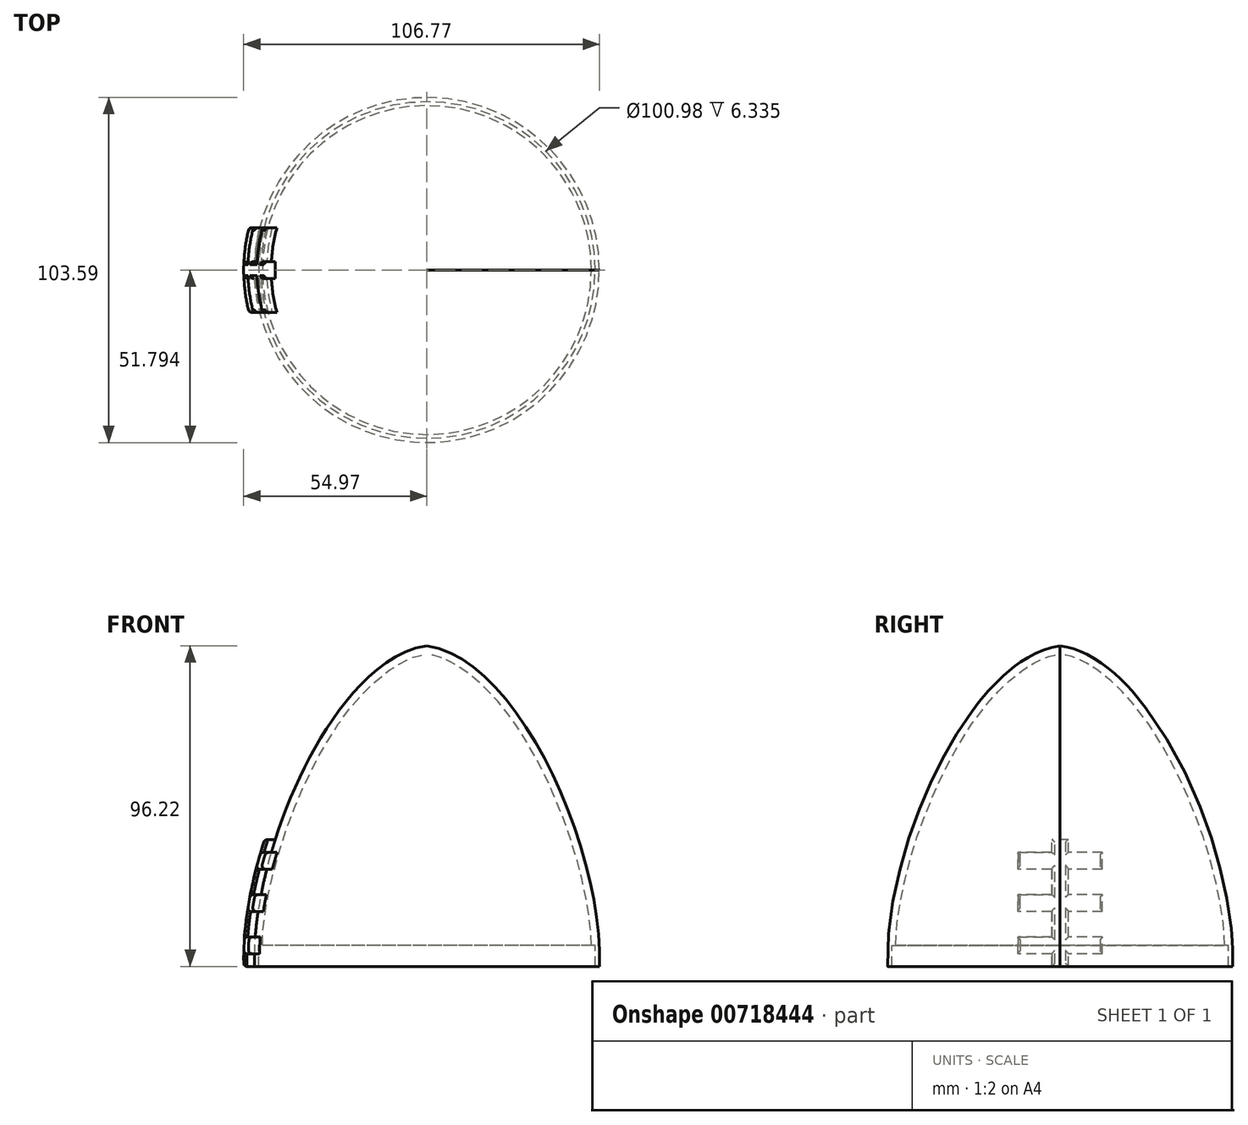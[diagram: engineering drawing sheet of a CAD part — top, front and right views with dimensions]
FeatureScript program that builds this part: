
annotation { "Feature Type Name" : "Feature", "Feature Type Description" : "" }
export const myFeature = defineFeature(function(context is Context, id is Id, definition is map)
    precondition{}
    {
        {
            var Q0;
            Q0=qCreatedBy(makeId("Front.planeOp"),FACE);
            var sketch = newSketch(context, id + "F0", { "sketchPlane" : qUnion([Q0])});
            skFitSpline(sketch, "E0", {"points": [v(40.85, 0) * mm, v(0, 75.94) * mm], "startDerivative": vector(2.97, 83.82) * mm, "endDerivative": vector(-64.34, 8.5) * mm});
            skFitSpline(sketch, "E1.0", {"points": [v(38.85, 0.07) * mm, v(38.97, 3.43) * mm, v(38.56, 10.75) * mm, v(36.21, 22.71) * mm, v(32.35, 34.94) * mm, v(27.22, 46.68) * mm, v(21.08, 57.23) * mm, v(15.35, 64.42) * mm, v(10.56, 68.85) * mm, v(6.92, 71.43) * mm, v(3.3, 73.2) * mm, v(0.92, 73.8) * mm, v(-0.26, 73.96) * mm]});
            skLineSegment(sketch, "E2", {"start": v(0, 75.94) * mm, "end": v(0, 73.92) * mm});
            skLineSegment(sketch, "E3", {"start": v(40.85, 0) * mm, "end": v(38.85, 0) * mm});
            skLineSegment(sketch, "E4", {"start": v(38.85, 0.07) * mm, "end": v(38.85, 0) * mm});
            skLineSegment(sketch, "E5", {"start": v(0, 73.92) * mm, "end": v(0, 73.92) * mm});
            skLineSegment(sketch, "E6", {"start": v(0, 77.78) * mm, "end": v(0, 26.3) * mm, "construction": true});
            skPoint(sketch, "E6.endSnap0", {"position": v(0, 74.93) * mm});
            skLineSegment(sketch, "E7", {"start": v(39.85, 0) * mm, "end": v(39.85, 5) * mm});
            skLineSegment(sketch, "E8", {"start": v(39.85, 5) * mm, "end": v(38.77, 5) * mm});
            skSolve(sketch);
        }
        {
            var Q0;
            Q0=makeQuery(id+"F0.imprint","IMPRINT",FACE,{"disambiguationData":[TD([[makeQuery(id+"F0.imprint","IMPRINT",EDGE,{"derivedFrom":sQuery(id+"F0.wireOp",EDGE,"E0")}),1.0]])]});
            var Q1;
            Q1=sQuery(id+"F0.wireOp",EDGE,"E6");
            revolve(context, id + "F1", {"surfaceOperationType" : NewSurfaceOperationType.NEW, "entities" : qUnion([Q0]), "axis" : qUnion([Q1]), "revolveType" : RevolveType.FULL});
        }
        {
            var Q0;
            {var subQ1=sQuery(id+"F0.wireOp",EDGE,"E4");Q0=makeQuery(id+"F0.imprint","IMPRINT",FACE,{"disambiguationData":[TD([[makeQuery(id+"F0.imprint","IMPRINT",EDGE,{"derivedFrom":subQ1}),1.0]])]});}
            var Q1;
            Q1=sQuery(id+"F0.wireOp",EDGE,"E6");
            revolve(context, id + "F2", {"operationType" : NewBodyOperationType.REMOVE, "surfaceOperationType" : NewSurfaceOperationType.NEW, "entities" : qUnion([Q0]), "axis" : qUnion([Q1]), "revolveType" : RevolveType.FULL, "oppositeDirection" : true});
        }
        {
            var Q0;
            Q0=qCreatedBy(makeId("Right.planeOp"),FACE);
            var sketch = newSketch(context, id + "F3", { "sketchPlane" : qUnion([Q0])});
            skLineSegment(sketch, "E9", {"start": v(2, 0) * mm, "end": v(2, 30) * mm});
            skLineSegment(sketch, "E10", {"start": v(2, 30) * mm, "end": v(0, 30) * mm});
            skLineSegment(sketch, "E11.MirrorCS", {"start": v(-2, 0) * mm, "end": v(-2, 30) * mm});
            skLineSegment(sketch, "E12.MirrorCS", {"start": v(-2, 30) * mm, "end": v(0, 30) * mm});
            skLineSegment(sketch, "E13", {"start": v(2, 3) * mm, "end": v(10, 3) * mm});
            skLineSegment(sketch, "E14", {"start": v(10, 3) * mm, "end": v(10, 7) * mm});
            skLineSegment(sketch, "E15", {"start": v(10, 7) * mm, "end": v(2, 7) * mm});
            skLineSegment(sketch, "E16.MirrorCS", {"start": v(-10, 7) * mm, "end": v(-2, 7) * mm});
            skLineSegment(sketch, "E17.MirrorCS", {"start": v(-10, 3) * mm, "end": v(-10, 7) * mm});
            skLineSegment(sketch, "E18.MirrorCS", {"start": v(-2, 3) * mm, "end": v(-10, 3) * mm});
            skLineSegment(sketch, "E19", {"start": v(2, 13) * mm, "end": v(10, 13) * mm});
            skLineSegment(sketch, "E20", {"start": v(10, 13) * mm, "end": v(10, 17) * mm});
            skLineSegment(sketch, "E21", {"start": v(10, 17) * mm, "end": v(2, 17) * mm});
            skLineSegment(sketch, "E22.MirrorCS", {"start": v(-10, 17) * mm, "end": v(-2, 17) * mm});
            skLineSegment(sketch, "E23.MirrorCS", {"start": v(-10, 13) * mm, "end": v(-10, 17) * mm});
            skLineSegment(sketch, "E24.MirrorCS", {"start": v(-2, 13) * mm, "end": v(-10, 13) * mm});
            skLineSegment(sketch, "E25", {"start": v(2, 23) * mm, "end": v(10, 23) * mm});
            skLineSegment(sketch, "E26", {"start": v(10, 23) * mm, "end": v(10, 27) * mm});
            skLineSegment(sketch, "E27", {"start": v(10, 27) * mm, "end": v(2, 27) * mm});
            skLineSegment(sketch, "E28.MirrorCS", {"start": v(-10, 27) * mm, "end": v(-2, 27) * mm});
            skLineSegment(sketch, "E29.MirrorCS", {"start": v(-2, 23) * mm, "end": v(-10, 23) * mm});
            skLineSegment(sketch, "E30.MirrorCS", {"start": v(-10, 23) * mm, "end": v(-10, 27) * mm});
            skLineSegment(sketch, "E31", {"start": v(-2, 0) * mm, "end": v(2, 0) * mm});
            skSolve(sketch);
        }
        {
            var Q0;
            {var subQ0=sQuery(id+"F3.wireOp",EDGE,"E13");Q0=makeQuery(id+"F3.imprint","IMPRINT",FACE,{"disambiguationData":[TD([[makeQuery(id+"F3.imprint","IMPRINT",EDGE,{"derivedFrom":subQ0}),1.0]])]});}
            var Q1;
            {var subQ4=sQuery(id+"F3.wireOp",EDGE,"E10");Q1=makeQuery(id+"F3.imprint","IMPRINT",FACE,{"disambiguationData":[TD([[makeQuery(id+"F3.imprint","IMPRINT",EDGE,{"derivedFrom":subQ4}),1.0]])]});}
            var Q2;
            {var subQ0=sQuery(id+"F3.wireOp",EDGE,"E16.MirrorCS");Q2=makeQuery(id+"F3.imprint","IMPRINT",FACE,{"disambiguationData":[TD([[makeQuery(id+"F3.imprint","IMPRINT",EDGE,{"derivedFrom":subQ0}),-1.0]])]});}
            var Q3;
            {var subQ0=sQuery(id+"F3.wireOp",EDGE,"E22.MirrorCS");Q3=makeQuery(id+"F3.imprint","IMPRINT",FACE,{"disambiguationData":[TD([[makeQuery(id+"F3.imprint","IMPRINT",EDGE,{"derivedFrom":subQ0}),-1.0]])]});}
            var Q4;
            {var subQ0=sQuery(id+"F3.wireOp",EDGE,"E19");Q4=makeQuery(id+"F3.imprint","IMPRINT",FACE,{"disambiguationData":[TD([[makeQuery(id+"F3.imprint","IMPRINT",EDGE,{"derivedFrom":subQ0}),1.0]])]});}
            var Q5;
            {var subQ0=sQuery(id+"F3.wireOp",EDGE,"E25");Q5=makeQuery(id+"F3.imprint","IMPRINT",FACE,{"disambiguationData":[TD([[makeQuery(id+"F3.imprint","IMPRINT",EDGE,{"derivedFrom":subQ0}),1.0]])]});}
            var Q6;
            {var subQ0=sQuery(id+"F3.wireOp",EDGE,"E28.MirrorCS");Q6=makeQuery(id+"F3.imprint","IMPRINT",FACE,{"disambiguationData":[TD([[makeQuery(id+"F3.imprint","IMPRINT",EDGE,{"derivedFrom":subQ0}),-1.0]])]});}
            var Q7;
            Q7=makeQuery(id+"F1.opRevolve","SWEPT_FACE",FACE,{"disambiguationData":[OSD([sQuery(id+"F0.wireOp",EDGE,"E0")])]});
            var Q8;
            Q8=makeQuery(id+"F1.opRevolve","SWEPT_BODY",BODY,{"disambiguationData":[OSD([sQuery(id+"F0.wireOp",EDGE,"E0"),sQuery(id+"F0.wireOp",EDGE,"E1.0"),sQuery(id+"F0.wireOp",EDGE,"E2"),sQuery(id+"F0.wireOp",EDGE,"E3"),sQuery(id+"F0.wireOp",EDGE,"E4"),sQuery(id+"F0.wireOp",EDGE,"E5")])]});
            extrude(context, id + "F4", {"entities" : qUnion([Q0, Q1, Q2, Q3, Q4, Q5, Q6]), "operationType" : NewBodyOperationType.ADD, "endBound" : BoundingType.UP_TO_SURFACE, "oppositeDirection" : true, "depth" : 25 * mm, "endBoundEntityFace" : qUnion([Q7]), "hasOffset" : true, "offsetDistance" : 2.5 * mm, "offsetOppositeDirection" : true, "hasSecondDirection" : true, "secondDirectionBound" : SecondDirectionBoundingType.UP_TO_BODY, "secondDirectionOppositeDirection" : true, "secondDirectionDepth" : 25 * mm, "secondDirectionBoundEntityBody" : qUnion([Q8])});
        }
        {
            var Q0;
            Q0=makeQuery(id+"F4.opExtrude","CAP_EDGE",EDGE,{"disambiguationData":[OSD([sQuery(id+"F3.wireOp",EDGE,"E13")]),topologyDisambiguationEdgeConnected([makeQuery(id+"F1.opRevolve","SWEPT_FACE",FACE,{"disambiguationData":[OSD([sQuery(id+"F0.wireOp",EDGE,"E0")])]})])],"isStart":false});
            var Q1;
            Q1=makeQuery(id+"F4.opExtrude","CAP_EDGE",EDGE,{"disambiguationData":[OSD([sQuery(id+"F3.wireOp",EDGE,"E15")]),topologyDisambiguationEdgeConnected([makeQuery(id+"F1.opRevolve","SWEPT_FACE",FACE,{"disambiguationData":[OSD([sQuery(id+"F0.wireOp",EDGE,"E0")])]})])],"isStart":false});
            var Q2;
            Q2=makeQuery(id+"F4.opExtrude","CAP_EDGE",EDGE,{"disambiguationData":[OSD([sQuery(id+"F3.wireOp",EDGE,"E14")]),topologyDisambiguationEdgeConnected([makeQuery(id+"F1.opRevolve","SWEPT_FACE",FACE,{"disambiguationData":[OSD([sQuery(id+"F0.wireOp",EDGE,"E0")])]})])],"isStart":false});
            var Q3;
            Q3=makeQuery(id+"F4.opExtrude","CAP_EDGE",EDGE,{"disambiguationData":[OSD([sQuery(id+"F3.wireOp",EDGE,"E18.MirrorCS")]),topologyDisambiguationEdgeConnected([makeQuery(id+"F1.opRevolve","SWEPT_FACE",FACE,{"disambiguationData":[OSD([sQuery(id+"F0.wireOp",EDGE,"E0")])]})])],"isStart":false});
            var Q4;
            Q4=makeQuery(id+"F4.opExtrude","CAP_EDGE",EDGE,{"disambiguationData":[OSD([sQuery(id+"F3.wireOp",EDGE,"E17.MirrorCS")]),topologyDisambiguationEdgeConnected([makeQuery(id+"F1.opRevolve","SWEPT_FACE",FACE,{"disambiguationData":[OSD([sQuery(id+"F0.wireOp",EDGE,"E0")])]})])],"isStart":false});
            var Q5;
            Q5=makeQuery(id+"F4.opExtrude","CAP_EDGE",EDGE,{"disambiguationData":[OSD([sQuery(id+"F3.wireOp",EDGE,"E16.MirrorCS")]),topologyDisambiguationEdgeConnected([makeQuery(id+"F1.opRevolve","SWEPT_FACE",FACE,{"disambiguationData":[OSD([sQuery(id+"F0.wireOp",EDGE,"E0")])]})])],"isStart":false});
            var Q6;
            {var subQ0=sQuery(id+"F3.wireOp",EDGE,"E11.MirrorCS");Q6=makeQuery(id+"F4.opExtrude","CAP_EDGE",EDGE,{"disambiguationData":[OSD([subQ0]),TDD([makeQuery(id+"F3.imprint","IMPRINT",EDGE,{"disambiguationData":[TD([[makeQuery(id+"F3.imprint","INTERSECT",VERTEX,{"derivedFrom":[subQ0,sQuery(id+"F3.wireOp",EDGE,"E16.MirrorCS")]}),-1.0]])],"derivedFrom":subQ0})]),topologyDisambiguationEdgeConnected([makeQuery(id+"F1.opRevolve","SWEPT_FACE",FACE,{"disambiguationData":[OSD([sQuery(id+"F0.wireOp",EDGE,"E0")])]})])],"isStart":false});}
            var Q7;
            {var subQ0=sQuery(id+"F3.wireOp",EDGE,"E11.MirrorCS");Q7=makeQuery(id+"F4.opExtrude","CAP_EDGE",EDGE,{"disambiguationData":[OSD([subQ0]),TDD([makeQuery(id+"F3.imprint","IMPRINT",EDGE,{"disambiguationData":[TD([[makeQuery(id+"F3.imprint","INTERSECT",VERTEX,{"derivedFrom":[subQ0,sQuery(id+"F3.wireOp",EDGE,"E31")]}),-1.0]])],"derivedFrom":subQ0})]),topologyDisambiguationEdgeConnected([makeQuery(id+"F1.opRevolve","SWEPT_FACE",FACE,{"disambiguationData":[OSD([sQuery(id+"F0.wireOp",EDGE,"E0")])]})])],"isStart":false});}
            var Q8;
            {var subQ0=sQuery(id+"F3.wireOp",EDGE,"E9");Q8=makeQuery(id+"F4.opExtrude","CAP_EDGE",EDGE,{"disambiguationData":[OSD([subQ0]),TDD([makeQuery(id+"F3.imprint","IMPRINT",EDGE,{"disambiguationData":[TD([[makeQuery(id+"F3.imprint","INTERSECT",VERTEX,{"derivedFrom":[subQ0,sQuery(id+"F3.wireOp",EDGE,"E31")]}),-1.0]])],"derivedFrom":subQ0})]),topologyDisambiguationEdgeConnected([makeQuery(id+"F1.opRevolve","SWEPT_FACE",FACE,{"disambiguationData":[OSD([sQuery(id+"F0.wireOp",EDGE,"E0")])]})])],"isStart":false});}
            var Q9;
            {var subQ0=sQuery(id+"F3.wireOp",EDGE,"E9");Q9=makeQuery(id+"F4.opExtrude","CAP_EDGE",EDGE,{"disambiguationData":[OSD([subQ0]),TDD([makeQuery(id+"F3.imprint","IMPRINT",EDGE,{"disambiguationData":[TD([[makeQuery(id+"F3.imprint","INTERSECT",VERTEX,{"derivedFrom":[subQ0,sQuery(id+"F3.wireOp",EDGE,"E15")]}),-1.0]])],"derivedFrom":subQ0})]),topologyDisambiguationEdgeConnected([makeQuery(id+"F1.opRevolve","SWEPT_FACE",FACE,{"disambiguationData":[OSD([sQuery(id+"F0.wireOp",EDGE,"E0")])]})])],"isStart":false});}
            var Q10;
            Q10=makeQuery(id+"F4.opExtrude","CAP_EDGE",EDGE,{"disambiguationData":[OSD([sQuery(id+"F3.wireOp",EDGE,"E19")]),topologyDisambiguationEdgeConnected([makeQuery(id+"F1.opRevolve","SWEPT_FACE",FACE,{"disambiguationData":[OSD([sQuery(id+"F0.wireOp",EDGE,"E0")])]})])],"isStart":false});
            var Q11;
            Q11=makeQuery(id+"F4.opExtrude","CAP_EDGE",EDGE,{"disambiguationData":[OSD([sQuery(id+"F3.wireOp",EDGE,"E20")]),topologyDisambiguationEdgeConnected([makeQuery(id+"F1.opRevolve","SWEPT_FACE",FACE,{"disambiguationData":[OSD([sQuery(id+"F0.wireOp",EDGE,"E0")])]})])],"isStart":false});
            var Q12;
            Q12=makeQuery(id+"F4.opExtrude","CAP_EDGE",EDGE,{"disambiguationData":[OSD([sQuery(id+"F3.wireOp",EDGE,"E21")]),topologyDisambiguationEdgeConnected([makeQuery(id+"F1.opRevolve","SWEPT_FACE",FACE,{"disambiguationData":[OSD([sQuery(id+"F0.wireOp",EDGE,"E0")])]})])],"isStart":false});
            var Q13;
            {var subQ0=sQuery(id+"F3.wireOp",EDGE,"E9");Q13=makeQuery(id+"F4.opExtrude","CAP_EDGE",EDGE,{"disambiguationData":[OSD([subQ0]),TDD([makeQuery(id+"F3.imprint","IMPRINT",EDGE,{"disambiguationData":[TD([[makeQuery(id+"F3.imprint","INTERSECT",VERTEX,{"derivedFrom":[subQ0,sQuery(id+"F3.wireOp",EDGE,"E21")]}),-1.0]])],"derivedFrom":subQ0})]),topologyDisambiguationEdgeConnected([makeQuery(id+"F1.opRevolve","SWEPT_FACE",FACE,{"disambiguationData":[OSD([sQuery(id+"F0.wireOp",EDGE,"E0")])]})])],"isStart":false});}
            var Q14;
            Q14=makeQuery(id+"F4.opExtrude","CAP_EDGE",EDGE,{"disambiguationData":[OSD([sQuery(id+"F3.wireOp",EDGE,"E24.MirrorCS")]),topologyDisambiguationEdgeConnected([makeQuery(id+"F1.opRevolve","SWEPT_FACE",FACE,{"disambiguationData":[OSD([sQuery(id+"F0.wireOp",EDGE,"E0")])]})])],"isStart":false});
            var Q15;
            Q15=makeQuery(id+"F4.opExtrude","CAP_EDGE",EDGE,{"disambiguationData":[OSD([sQuery(id+"F3.wireOp",EDGE,"E22.MirrorCS")]),topologyDisambiguationEdgeConnected([makeQuery(id+"F1.opRevolve","SWEPT_FACE",FACE,{"disambiguationData":[OSD([sQuery(id+"F0.wireOp",EDGE,"E0")])]})])],"isStart":false});
            var Q16;
            Q16=makeQuery(id+"F4.opExtrude","CAP_EDGE",EDGE,{"disambiguationData":[OSD([sQuery(id+"F3.wireOp",EDGE,"E23.MirrorCS")]),topologyDisambiguationEdgeConnected([makeQuery(id+"F1.opRevolve","SWEPT_FACE",FACE,{"disambiguationData":[OSD([sQuery(id+"F0.wireOp",EDGE,"E0")])]})])],"isStart":false});
            var Q17;
            {var subQ0=sQuery(id+"F3.wireOp",EDGE,"E11.MirrorCS");Q17=makeQuery(id+"F4.opExtrude","CAP_EDGE",EDGE,{"disambiguationData":[OSD([subQ0]),TDD([makeQuery(id+"F3.imprint","IMPRINT",EDGE,{"disambiguationData":[TD([[makeQuery(id+"F3.imprint","INTERSECT",VERTEX,{"derivedFrom":[subQ0,sQuery(id+"F3.wireOp",EDGE,"E22.MirrorCS")]}),-1.0]])],"derivedFrom":subQ0})]),topologyDisambiguationEdgeConnected([makeQuery(id+"F1.opRevolve","SWEPT_FACE",FACE,{"disambiguationData":[OSD([sQuery(id+"F0.wireOp",EDGE,"E0")])]})])],"isStart":false});}
            var Q18;
            Q18=makeQuery(id+"F4.opExtrude","CAP_EDGE",EDGE,{"disambiguationData":[OSD([sQuery(id+"F3.wireOp",EDGE,"E25")]),topologyDisambiguationEdgeConnected([makeQuery(id+"F1.opRevolve","SWEPT_FACE",FACE,{"disambiguationData":[OSD([sQuery(id+"F0.wireOp",EDGE,"E0")])]})])],"isStart":false});
            var Q19;
            Q19=makeQuery(id+"F4.opExtrude","CAP_EDGE",EDGE,{"disambiguationData":[OSD([sQuery(id+"F3.wireOp",EDGE,"E27")]),topologyDisambiguationEdgeConnected([makeQuery(id+"F1.opRevolve","SWEPT_FACE",FACE,{"disambiguationData":[OSD([sQuery(id+"F0.wireOp",EDGE,"E0")])]})])],"isStart":false});
            var Q20;
            {var subQ0=sQuery(id+"F3.wireOp",EDGE,"E9");Q20=makeQuery(id+"F4.opExtrude","CAP_EDGE",EDGE,{"disambiguationData":[OSD([subQ0]),TDD([makeQuery(id+"F3.imprint","IMPRINT",EDGE,{"disambiguationData":[TD([[makeQuery(id+"F3.imprint","INTERSECT",VERTEX,{"derivedFrom":[subQ0,sQuery(id+"F3.wireOp",EDGE,"E10")]}),1.0]])],"derivedFrom":subQ0})]),topologyDisambiguationEdgeConnected([makeQuery(id+"F1.opRevolve","SWEPT_FACE",FACE,{"disambiguationData":[OSD([sQuery(id+"F0.wireOp",EDGE,"E0")])]})])],"isStart":false});}
            var Q21;
            Q21=makeQuery(id+"F4.opExtrude","CAP_EDGE",EDGE,{"disambiguationData":[OSD([sQuery(id+"F3.wireOp",EDGE,"E10"),sQuery(id+"F3.wireOp",EDGE,"E12.MirrorCS")]),topologyDisambiguationEdgeConnected([makeQuery(id+"F1.opRevolve","SWEPT_FACE",FACE,{"disambiguationData":[OSD([sQuery(id+"F0.wireOp",EDGE,"E0")])]})])],"isStart":false});
            var Q22;
            {var subQ0=sQuery(id+"F3.wireOp",EDGE,"E11.MirrorCS");Q22=makeQuery(id+"F4.opExtrude","CAP_EDGE",EDGE,{"disambiguationData":[OSD([subQ0]),TDD([makeQuery(id+"F3.imprint","IMPRINT",EDGE,{"disambiguationData":[TD([[makeQuery(id+"F3.imprint","INTERSECT",VERTEX,{"derivedFrom":[subQ0,sQuery(id+"F3.wireOp",EDGE,"E12.MirrorCS")]}),1.0]])],"derivedFrom":subQ0})]),topologyDisambiguationEdgeConnected([makeQuery(id+"F1.opRevolve","SWEPT_FACE",FACE,{"disambiguationData":[OSD([sQuery(id+"F0.wireOp",EDGE,"E0")])]})])],"isStart":false});}
            var Q23;
            Q23=makeQuery(id+"F4.opExtrude","CAP_EDGE",EDGE,{"disambiguationData":[OSD([sQuery(id+"F3.wireOp",EDGE,"E28.MirrorCS")]),topologyDisambiguationEdgeConnected([makeQuery(id+"F1.opRevolve","SWEPT_FACE",FACE,{"disambiguationData":[OSD([sQuery(id+"F0.wireOp",EDGE,"E0")])]})])],"isStart":false});
            var Q24;
            Q24=makeQuery(id+"F4.opExtrude","CAP_EDGE",EDGE,{"disambiguationData":[OSD([sQuery(id+"F3.wireOp",EDGE,"E30.MirrorCS")]),topologyDisambiguationEdgeConnected([makeQuery(id+"F1.opRevolve","SWEPT_FACE",FACE,{"disambiguationData":[OSD([sQuery(id+"F0.wireOp",EDGE,"E0")])]})])],"isStart":false});
            var Q25;
            Q25=makeQuery(id+"F4.opExtrude","CAP_EDGE",EDGE,{"disambiguationData":[OSD([sQuery(id+"F3.wireOp",EDGE,"E29.MirrorCS")]),topologyDisambiguationEdgeConnected([makeQuery(id+"F1.opRevolve","SWEPT_FACE",FACE,{"disambiguationData":[OSD([sQuery(id+"F0.wireOp",EDGE,"E0")])]})])],"isStart":false});
            var Q26;
            Q26=makeQuery(id+"F4.opExtrude","TWEAK_EDGE",EDGE,{"derivedFrom":[makeQuery(id+"F3.imprint","IMPRINT",EDGE,{"derivedFrom":sQuery(id+"F3.wireOp",EDGE,"E14")}),makeQuery(id+"F3.imprint","IMPRINT",EDGE,{"derivedFrom":sQuery(id+"F3.wireOp",EDGE,"E15")})]});
            var Q27;
            Q27=makeQuery(id+"F4.opExtrude","TWEAK_EDGE",EDGE,{"derivedFrom":[makeQuery(id+"F3.imprint","IMPRINT",EDGE,{"derivedFrom":sQuery(id+"F3.wireOp",EDGE,"E13")}),makeQuery(id+"F3.imprint","IMPRINT",EDGE,{"derivedFrom":sQuery(id+"F3.wireOp",EDGE,"E14")})]});
            var Q28;
            Q28=makeQuery(id+"F4.opExtrude","TWEAK_EDGE",EDGE,{"derivedFrom":[makeQuery(id+"F3.imprint","IMPRINT",EDGE,{"derivedFrom":sQuery(id+"F3.wireOp",EDGE,"E19")}),makeQuery(id+"F3.imprint","IMPRINT",EDGE,{"derivedFrom":sQuery(id+"F3.wireOp",EDGE,"E20")})]});
            var Q29;
            Q29=makeQuery(id+"F4.opExtrude","TWEAK_EDGE",EDGE,{"derivedFrom":[makeQuery(id+"F3.imprint","IMPRINT",EDGE,{"derivedFrom":sQuery(id+"F3.wireOp",EDGE,"E20")}),makeQuery(id+"F3.imprint","IMPRINT",EDGE,{"derivedFrom":sQuery(id+"F3.wireOp",EDGE,"E21")})]});
            var Q30;
            Q30=makeQuery(id+"F4.opExtrude","TWEAK_EDGE",EDGE,{"derivedFrom":[makeQuery(id+"F3.imprint","IMPRINT",EDGE,{"derivedFrom":sQuery(id+"F3.wireOp",EDGE,"E25")}),makeQuery(id+"F3.imprint","IMPRINT",EDGE,{"derivedFrom":sQuery(id+"F3.wireOp",EDGE,"E26")})]});
            var Q31;
            Q31=makeQuery(id+"F4.opExtrude","TWEAK_EDGE",EDGE,{"derivedFrom":[makeQuery(id+"F3.imprint","IMPRINT",EDGE,{"derivedFrom":sQuery(id+"F3.wireOp",EDGE,"E26")}),makeQuery(id+"F3.imprint","IMPRINT",EDGE,{"derivedFrom":sQuery(id+"F3.wireOp",EDGE,"E27")})]});
            var Q32;
            {var subQ0=sQuery(id+"F3.wireOp",EDGE,"E10");var subQ1=sQuery(id+"F3.wireOp",EDGE,"E9");Q32=makeQuery(id+"F4.opExtrude","TWEAK_EDGE",EDGE,{"derivedFrom":[makeQuery(id+"F3.imprint","IMPRINT",EDGE,{"disambiguationData":[TD([[makeQuery(id+"F3.imprint","INTERSECT",VERTEX,{"derivedFrom":[subQ1,subQ0]}),1.0]])],"derivedFrom":subQ1}),makeQuery(id+"F3.imprint","IMPRINT",EDGE,{"derivedFrom":subQ0}),makeQuery(id+"F3.imprint","IMPRINT",EDGE,{"derivedFrom":sQuery(id+"F3.wireOp",EDGE,"E12.MirrorCS")})]});}
            var Q33;
            {var subQ0=sQuery(id+"F3.wireOp",EDGE,"E21");var subQ1=sQuery(id+"F3.wireOp",EDGE,"E9");Q33=makeQuery(id+"F4.opExtrude","TWEAK_EDGE",EDGE,{"derivedFrom":[makeQuery(id+"F3.imprint","IMPRINT",EDGE,{"disambiguationData":[TD([[makeQuery(id+"F3.imprint","INTERSECT",VERTEX,{"derivedFrom":[subQ1,subQ0]}),-1.0]])],"derivedFrom":subQ1}),makeQuery(id+"F3.imprint","IMPRINT",EDGE,{"derivedFrom":subQ0})]});}
            var Q34;
            {var subQ0=sQuery(id+"F3.wireOp",EDGE,"E15");var subQ1=sQuery(id+"F3.wireOp",EDGE,"E9");Q34=makeQuery(id+"F4.opExtrude","TWEAK_EDGE",EDGE,{"derivedFrom":[makeQuery(id+"F3.imprint","IMPRINT",EDGE,{"disambiguationData":[TD([[makeQuery(id+"F3.imprint","INTERSECT",VERTEX,{"derivedFrom":[subQ1,subQ0]}),-1.0]])],"derivedFrom":subQ1}),makeQuery(id+"F3.imprint","IMPRINT",EDGE,{"derivedFrom":subQ0})]});}
            var Q35;
            {var subQ0=sQuery(id+"F3.wireOp",EDGE,"E16.MirrorCS");var subQ1=sQuery(id+"F3.wireOp",EDGE,"E11.MirrorCS");Q35=makeQuery(id+"F4.opExtrude","TWEAK_EDGE",EDGE,{"derivedFrom":[makeQuery(id+"F3.imprint","IMPRINT",EDGE,{"disambiguationData":[TD([[makeQuery(id+"F3.imprint","INTERSECT",VERTEX,{"derivedFrom":[subQ1,subQ0]}),-1.0]])],"derivedFrom":subQ1}),makeQuery(id+"F3.imprint","IMPRINT",EDGE,{"derivedFrom":subQ0})]});}
            var Q36;
            Q36=makeQuery(id+"F4.opExtrude","TWEAK_EDGE",EDGE,{"derivedFrom":[makeQuery(id+"F3.imprint","IMPRINT",EDGE,{"derivedFrom":sQuery(id+"F3.wireOp",EDGE,"E16.MirrorCS")}),makeQuery(id+"F3.imprint","IMPRINT",EDGE,{"derivedFrom":sQuery(id+"F3.wireOp",EDGE,"E17.MirrorCS")})]});
            var Q37;
            Q37=makeQuery(id+"F4.opExtrude","TWEAK_EDGE",EDGE,{"derivedFrom":[makeQuery(id+"F3.imprint","IMPRINT",EDGE,{"derivedFrom":sQuery(id+"F3.wireOp",EDGE,"E17.MirrorCS")}),makeQuery(id+"F3.imprint","IMPRINT",EDGE,{"derivedFrom":sQuery(id+"F3.wireOp",EDGE,"E18.MirrorCS")})]});
            var Q38;
            {var subQ0=sQuery(id+"F3.wireOp",EDGE,"E18.MirrorCS");var subQ1=sQuery(id+"F3.wireOp",EDGE,"E11.MirrorCS");Q38=makeQuery(id+"F4.opExtrude","TWEAK_EDGE",EDGE,{"derivedFrom":[makeQuery(id+"F3.imprint","IMPRINT",EDGE,{"disambiguationData":[TD([[makeQuery(id+"F3.imprint","INTERSECT",VERTEX,{"derivedFrom":[subQ1,sQuery(id+"F3.wireOp",EDGE,"E31")]}),-1.0]])],"derivedFrom":subQ1}),makeQuery(id+"F3.imprint","IMPRINT",EDGE,{"derivedFrom":subQ0})]});}
            var Q39;
            {var subQ0=sQuery(id+"F3.wireOp",EDGE,"E22.MirrorCS");var subQ1=sQuery(id+"F3.wireOp",EDGE,"E11.MirrorCS");Q39=makeQuery(id+"F4.opExtrude","TWEAK_EDGE",EDGE,{"derivedFrom":[makeQuery(id+"F3.imprint","IMPRINT",EDGE,{"disambiguationData":[TD([[makeQuery(id+"F3.imprint","INTERSECT",VERTEX,{"derivedFrom":[subQ1,subQ0]}),-1.0]])],"derivedFrom":subQ1}),makeQuery(id+"F3.imprint","IMPRINT",EDGE,{"derivedFrom":subQ0})]});}
            var Q40;
            {var subQ0=sQuery(id+"F3.wireOp",EDGE,"E29.MirrorCS");var subQ1=sQuery(id+"F3.wireOp",EDGE,"E11.MirrorCS");Q40=makeQuery(id+"F4.opExtrude","TWEAK_EDGE",EDGE,{"derivedFrom":[makeQuery(id+"F3.imprint","IMPRINT",EDGE,{"disambiguationData":[TD([[makeQuery(id+"F3.imprint","INTERSECT",VERTEX,{"derivedFrom":[subQ1,sQuery(id+"F3.wireOp",EDGE,"E22.MirrorCS")]}),-1.0]])],"derivedFrom":subQ1}),makeQuery(id+"F3.imprint","IMPRINT",EDGE,{"derivedFrom":subQ0})]});}
            var Q41;
            {var subQ0=sQuery(id+"F3.wireOp",EDGE,"E28.MirrorCS");var subQ1=sQuery(id+"F3.wireOp",EDGE,"E11.MirrorCS");Q41=makeQuery(id+"F4.opExtrude","TWEAK_EDGE",EDGE,{"derivedFrom":[makeQuery(id+"F3.imprint","IMPRINT",EDGE,{"disambiguationData":[TD([[makeQuery(id+"F3.imprint","INTERSECT",VERTEX,{"derivedFrom":[subQ1,sQuery(id+"F3.wireOp",EDGE,"E12.MirrorCS")]}),1.0]])],"derivedFrom":subQ1}),makeQuery(id+"F3.imprint","IMPRINT",EDGE,{"derivedFrom":subQ0})]});}
            var Q42;
            {var subQ0=sQuery(id+"F3.wireOp",EDGE,"E12.MirrorCS");var subQ1=sQuery(id+"F3.wireOp",EDGE,"E11.MirrorCS");Q42=makeQuery(id+"F4.opExtrude","TWEAK_EDGE",EDGE,{"derivedFrom":[makeQuery(id+"F3.imprint","IMPRINT",EDGE,{"derivedFrom":sQuery(id+"F3.wireOp",EDGE,"E10")}),makeQuery(id+"F3.imprint","IMPRINT",EDGE,{"disambiguationData":[TD([[makeQuery(id+"F3.imprint","INTERSECT",VERTEX,{"derivedFrom":[subQ1,subQ0]}),1.0]])],"derivedFrom":subQ1}),makeQuery(id+"F3.imprint","IMPRINT",EDGE,{"derivedFrom":subQ0})]});}
            var Q43;
            Q43=makeQuery(id+"F4.opExtrude","TWEAK_EDGE",EDGE,{"derivedFrom":[makeQuery(id+"F3.imprint","IMPRINT",EDGE,{"derivedFrom":sQuery(id+"F3.wireOp",EDGE,"E28.MirrorCS")}),makeQuery(id+"F3.imprint","IMPRINT",EDGE,{"derivedFrom":sQuery(id+"F3.wireOp",EDGE,"E30.MirrorCS")})]});
            var Q44;
            Q44=makeQuery(id+"F4.opExtrude","TWEAK_EDGE",EDGE,{"derivedFrom":[makeQuery(id+"F3.imprint","IMPRINT",EDGE,{"derivedFrom":sQuery(id+"F3.wireOp",EDGE,"E29.MirrorCS")}),makeQuery(id+"F3.imprint","IMPRINT",EDGE,{"derivedFrom":sQuery(id+"F3.wireOp",EDGE,"E30.MirrorCS")})]});
            var Q45;
            Q45=makeQuery(id+"F4.opExtrude","CAP_EDGE",EDGE,{"disambiguationData":[OSD([sQuery(id+"F3.wireOp",EDGE,"E26")]),topologyDisambiguationEdgeConnected([makeQuery(id+"F1.opRevolve","SWEPT_FACE",FACE,{"disambiguationData":[OSD([sQuery(id+"F0.wireOp",EDGE,"E0")])]})])],"isStart":false});
            var Q46;
            {var subQ0=sQuery(id+"F3.wireOp",EDGE,"E27");var subQ1=sQuery(id+"F3.wireOp",EDGE,"E9");Q46=makeQuery(id+"F4.opExtrude","TWEAK_EDGE",EDGE,{"derivedFrom":[makeQuery(id+"F3.imprint","IMPRINT",EDGE,{"disambiguationData":[TD([[makeQuery(id+"F3.imprint","INTERSECT",VERTEX,{"derivedFrom":[subQ1,sQuery(id+"F3.wireOp",EDGE,"E10")]}),1.0]])],"derivedFrom":subQ1}),makeQuery(id+"F3.imprint","IMPRINT",EDGE,{"derivedFrom":subQ0})]});}
            var Q47;
            {var subQ0=sQuery(id+"F3.wireOp",EDGE,"E25");var subQ1=sQuery(id+"F3.wireOp",EDGE,"E9");Q47=makeQuery(id+"F4.opExtrude","TWEAK_EDGE",EDGE,{"derivedFrom":[makeQuery(id+"F3.imprint","IMPRINT",EDGE,{"disambiguationData":[TD([[makeQuery(id+"F3.imprint","INTERSECT",VERTEX,{"derivedFrom":[subQ1,sQuery(id+"F3.wireOp",EDGE,"E21")]}),-1.0]])],"derivedFrom":subQ1}),makeQuery(id+"F3.imprint","IMPRINT",EDGE,{"derivedFrom":subQ0})]});}
            var Q48;
            {var subQ0=sQuery(id+"F3.wireOp",EDGE,"E24.MirrorCS");var subQ1=sQuery(id+"F3.wireOp",EDGE,"E11.MirrorCS");Q48=makeQuery(id+"F4.opExtrude","TWEAK_EDGE",EDGE,{"derivedFrom":[makeQuery(id+"F3.imprint","IMPRINT",EDGE,{"disambiguationData":[TD([[makeQuery(id+"F3.imprint","INTERSECT",VERTEX,{"derivedFrom":[subQ1,sQuery(id+"F3.wireOp",EDGE,"E16.MirrorCS")]}),-1.0]])],"derivedFrom":subQ1}),makeQuery(id+"F3.imprint","IMPRINT",EDGE,{"derivedFrom":subQ0})]});}
            var Q49;
            {var subQ0=sQuery(id+"F3.wireOp",EDGE,"E19");var subQ1=sQuery(id+"F3.wireOp",EDGE,"E9");Q49=makeQuery(id+"F4.opExtrude","TWEAK_EDGE",EDGE,{"derivedFrom":[makeQuery(id+"F3.imprint","IMPRINT",EDGE,{"disambiguationData":[TD([[makeQuery(id+"F3.imprint","INTERSECT",VERTEX,{"derivedFrom":[subQ1,sQuery(id+"F3.wireOp",EDGE,"E15")]}),-1.0]])],"derivedFrom":subQ1}),makeQuery(id+"F3.imprint","IMPRINT",EDGE,{"derivedFrom":subQ0})]});}
            var Q50;
            {var subQ0=sQuery(id+"F3.wireOp",EDGE,"E13");var subQ1=sQuery(id+"F3.wireOp",EDGE,"E9");Q50=makeQuery(id+"F4.opExtrude","TWEAK_EDGE",EDGE,{"derivedFrom":[makeQuery(id+"F3.imprint","IMPRINT",EDGE,{"disambiguationData":[TD([[makeQuery(id+"F3.imprint","INTERSECT",VERTEX,{"derivedFrom":[subQ1,sQuery(id+"F3.wireOp",EDGE,"E31")]}),-1.0]])],"derivedFrom":subQ1}),makeQuery(id+"F3.imprint","IMPRINT",EDGE,{"derivedFrom":subQ0})]});}
            var Q51;
            Q51=makeQuery(id+"F4.opExtrude","TWEAK_EDGE",EDGE,{"derivedFrom":[makeQuery(id+"F3.imprint","IMPRINT",EDGE,{"derivedFrom":sQuery(id+"F3.wireOp",EDGE,"E23.MirrorCS")}),makeQuery(id+"F3.imprint","IMPRINT",EDGE,{"derivedFrom":sQuery(id+"F3.wireOp",EDGE,"E24.MirrorCS")})]});
            var Q52;
            Q52=makeQuery(id+"F4.opExtrude","TWEAK_EDGE",EDGE,{"derivedFrom":[makeQuery(id+"F3.imprint","IMPRINT",EDGE,{"derivedFrom":sQuery(id+"F3.wireOp",EDGE,"E22.MirrorCS")}),makeQuery(id+"F3.imprint","IMPRINT",EDGE,{"derivedFrom":sQuery(id+"F3.wireOp",EDGE,"E23.MirrorCS")})]});
            var Q53;
            Q53=makeQuery(id+"F4.opExtrude","CAP_EDGE",EDGE,{"disambiguationData":[OSD([sQuery(id+"F3.wireOp",EDGE,"E31")])],"isStart":false});
            var Q54;
            {var subQ0=sQuery(id+"F3.wireOp",EDGE,"E31");var subQ1=sQuery(id+"F3.wireOp",EDGE,"E11.MirrorCS");Q54=makeQuery(id+"F4.opExtrude","TWEAK_EDGE",EDGE,{"derivedFrom":[makeQuery(id+"F3.imprint","IMPRINT",EDGE,{"disambiguationData":[TD([[makeQuery(id+"F3.imprint","INTERSECT",VERTEX,{"derivedFrom":[subQ1,subQ0]}),-1.0]])],"derivedFrom":subQ1}),makeQuery(id+"F3.imprint","IMPRINT",EDGE,{"derivedFrom":subQ0})]});}
            var Q55;
            {var subQ0=sQuery(id+"F3.wireOp",EDGE,"E31");var subQ1=sQuery(id+"F3.wireOp",EDGE,"E9");Q55=makeQuery(id+"F4.opExtrude","TWEAK_EDGE",EDGE,{"derivedFrom":[makeQuery(id+"F3.imprint","IMPRINT",EDGE,{"disambiguationData":[TD([[makeQuery(id+"F3.imprint","INTERSECT",VERTEX,{"derivedFrom":[subQ1,subQ0]}),-1.0]])],"derivedFrom":subQ1}),makeQuery(id+"F3.imprint","IMPRINT",EDGE,{"derivedFrom":subQ0})]});}
            fillet(context, id + "F5", {"entities" : qUnion([Q0, Q1, Q2, Q3, Q4, Q5, Q6, Q7, Q8, Q9, Q10, Q11, Q12, Q13, Q14, Q15, Q16, Q17, Q18, Q19, Q20, Q21, Q22, Q23, Q24, Q25, Q26, Q27, Q28, Q29, Q30, Q31, Q32, Q33, Q34, Q35, Q36, Q37, Q38, Q39, Q40, Q41, Q42, Q43, Q44, Q45, Q46, Q47, Q48, Q49, Q50, Q51, Q52, Q53, Q54, Q55]), "radius" : .75 * mm, "tangentPropagation" : true, "allowEdgeOverflow" : false});
        }
        {
            var Q0;
            Q0=makeQuery(id+"F1.opRevolve","SWEPT_BODY",BODY,{"disambiguationData":[OSD([sQuery(id+"F0.wireOp",EDGE,"E0"),sQuery(id+"F0.wireOp",EDGE,"E1.0"),sQuery(id+"F0.wireOp",EDGE,"E2"),sQuery(id+"F0.wireOp",EDGE,"E3"),sQuery(id+"F0.wireOp",EDGE,"E5"),sQuery(id+"F0.wireOp",EDGE,"E7"),sQuery(id+"F0.wireOp",EDGE,"E8")])]});
            var Q1;
            Q1=sQuery(id+"F3.wireOp",VERTEX,"E31.start");
            transform(context, id + "F6", {"entities" : qUnion([Q0]), "transformType" : TransformType.SCALE_UNIFORMLY, "scale" : 1.27, "scalePoint" : qUnion([Q1]), "makeCopy" : false});
        }
    });
